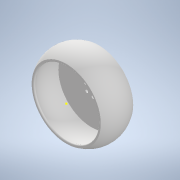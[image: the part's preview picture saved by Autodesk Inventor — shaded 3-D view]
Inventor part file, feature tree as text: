
AUTODESK INVENTOR PART (.ipt)
format: ipt  version: 2020 (Build 240168000, 168)  size: 250,368 bytes
history: native  units: mm
features: sketch x8, extrude x5, other x4, reference x2, sweep x1, shell x1, fillet x1, projected_geometry x1
ambient origin geometry x8: Origin, YZ Plane, XZ Plane, XY Plane, X Axis, Y Axis, Z Axis, Center Point
bodies: Solid1 (feature_tree)
feature tree (23):
  sweep  "Sweep1"
  shell  "Shell1"  Thickness=12.0mm
  extrude  "Extrusion1"  Depth=15.0mm
  extrude  "Extrusion2"  Depth=2.5mm
  extrude  "Extrusion3"  Depth=10.0mm
  fillet  "Fillet1"  Radius=10.0mm
  sketch  "Sketch8"  dims[d16=26.0mm d17=18.0mm]
  extrude  "Extrusion4"  Depth=1.0mm
  extrude  "Extrusion5"  Depth=18.0mm
  sketch  "Sketch1"  dims[d0=75.0mm d1=50.0mm d2=12.0mm]
  sketch  "Sketch2"  dims[d3=30.0mm d4=15.0mm]
  sketch  "Sketch4"  dims[d5=0.0mm d6=0.0mm d7=2.5mm]
  reference  "Reference1"
  reference  "Reference2"
  sketch  "Sketch6"  dims[d8=10.0mm d9=0.0mm d10=5.0mm d11=10.0mm d12=0.0mm]
  sketch  "Sketch7"  dims[d13=4.0mm d14=0.0mm d15=1.0mm]
  projected_geometry  "Projected Loop1"
  sketch  "Sketch9"  dims[d18=14.0mm d19=0.0mm]
  sketch  "Sketch10"  dims[d20=24.92mm d21=40.0mm d22=6.5mm d23=0.0mm]
  other  "<userpath>\Desktop\KangKangBalancing\KangKang.iam"
  other  "KangKang.iam"
  other  "tarot_5008_340kv_assy:1"
  other  "housing0:1"
